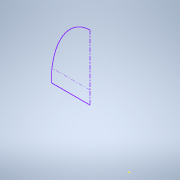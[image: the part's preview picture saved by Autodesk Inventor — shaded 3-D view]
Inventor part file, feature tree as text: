
AUTODESK INVENTOR PART (.ipt)
format: ipt  version: 2022 (Build 260153000, 153)  size: 86,528 bytes
history: native  units: in
note: dims shown in document units (in); Inventor stores cm internally (conversion verified against a paired STEP export)
features: sketch x1
ambient origin geometry x8: Origin, YZ Plane, XZ Plane, XY Plane, X Axis, Y Axis, Z Axis, Center Point
feature tree (1):
  sketch  "Sketch1"  dims[d3=0.0344in d4=0.0344in]
